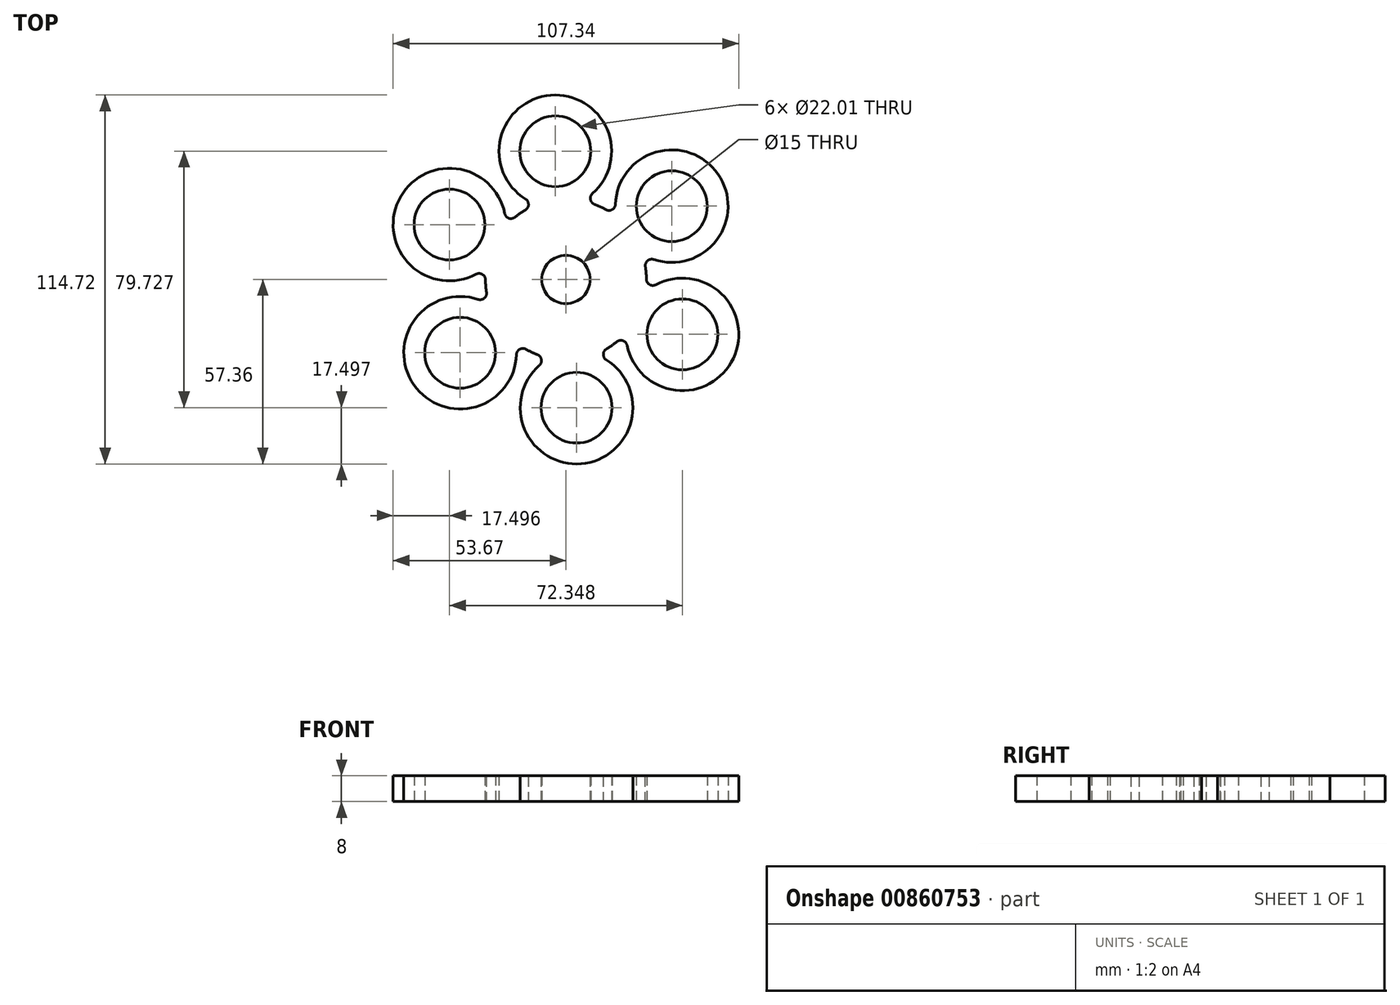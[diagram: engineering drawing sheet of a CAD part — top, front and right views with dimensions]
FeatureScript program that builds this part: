
annotation { "Feature Type Name" : "Feature", "Feature Type Description" : "" }
export const myFeature = defineFeature(function(context is Context, id is Id, definition is map)
    precondition{}
    {
        {
            var Q0;
            Q0=qCreatedBy(makeId("Top.planeOp"),FACE);
            var sketch = newSketch(context, id + "F0", { "sketchPlane" : qUnion([Q0])});
            skCircle(sketch, "E0", {"center": v(0, 0) * mm, "radius": 40 * mm, "construction": true});
            skCircle(sketch, "E1", {"center": v(0, 0) * mm, "radius": 7.5 * mm});
            skLineSegment(sketch, "E2.0", {"start": v(36.17, -17.07) * mm, "end": v(3.3, -39.86) * mm, "construction": true});
            skLineSegment(sketch, "E2.1", {"start": v(3.3, -39.86) * mm, "end": v(-32.87, -22.8) * mm, "construction": true});
            skLineSegment(sketch, "E2.2", {"start": v(-32.87, -22.8) * mm, "end": v(-36.17, 17.07) * mm, "construction": true});
            skLineSegment(sketch, "E2.3", {"start": v(-36.17, 17.07) * mm, "end": v(-3.3, 39.86) * mm, "construction": true});
            skLineSegment(sketch, "E2.4", {"start": v(-3.3, 39.86) * mm, "end": v(32.87, 22.8) * mm, "construction": true});
            skLineSegment(sketch, "E2.5", {"start": v(32.87, 22.8) * mm, "end": v(36.17, -17.07) * mm, "construction": true});
            skArc(sketch, "E3", {"start": v(5.05, 24.48) * mm, "mid": v(-4.75, 57.3) * mm, "end": v(-9, 23.32) * mm});
            skArc(sketch, "E4", {"start": v(-24.7, 3.86) * mm, "mid": v(-24.91, -2.06) * mm, "end": v(-23.73, -7.87) * mm});
            skArc(sketch, "E5.1.0", {"start": v(-18.68, 16.61) * mm, "mid": v(-52, 24.54) * mm, "end": v(-24.7, 3.86) * mm});
            skArc(sketch, "E5.2.0", {"start": v(-23.73, -7.87) * mm, "mid": v(-47.25, -32.76) * mm, "end": v(-15.7, -19.46) * mm});
            skArc(sketch, "E5.3.0", {"start": v(-5.05, -24.48) * mm, "mid": v(4.75, -57.3) * mm, "end": v(9, -23.32) * mm});
            skArc(sketch, "E5.4.0", {"start": v(18.68, -16.61) * mm, "mid": v(52, -24.54) * mm, "end": v(24.7, -3.86) * mm});
            skArc(sketch, "E5.5.0", {"start": v(23.73, 7.87) * mm, "mid": v(47.25, 32.76) * mm, "end": v(15.7, 19.46) * mm});
            skArc(sketch, "E6.trimOffspring", {"start": v(-9, 23.32) * mm, "mid": v(-14.24, 20.54) * mm, "end": v(-18.68, 16.61) * mm});
            skArc(sketch, "E7.trimOffspring", {"start": v(15.7, 19.46) * mm, "mid": v(10.67, 22.6) * mm, "end": v(5.05, 24.48) * mm});
            skArc(sketch, "E8.trimOffspring", {"start": v(24.7, -3.86) * mm, "mid": v(24.91, 2.06) * mm, "end": v(23.73, 7.87) * mm});
            skArc(sketch, "E9.trimOffspring", {"start": v(9, -23.32) * mm, "mid": v(14.24, -20.54) * mm, "end": v(18.68, -16.61) * mm});
            skArc(sketch, "E10.trimOffspring", {"start": v(-15.7, -19.46) * mm, "mid": v(-10.67, -22.6) * mm, "end": v(-5.05, -24.48) * mm});
            skCircle(sketch, "E11", {"center": v(-3.3, 39.86) * mm, "radius": 11 * mm});
            skCircle(sketch, "E12.1.0", {"center": v(-36.17, 17.07) * mm, "radius": 11 * mm});
            skCircle(sketch, "E12.2.0", {"center": v(-32.87, -22.8) * mm, "radius": 11 * mm});
            skCircle(sketch, "E12.3.0", {"center": v(3.3, -39.86) * mm, "radius": 11 * mm});
            skCircle(sketch, "E12.4.0", {"center": v(36.17, -17.07) * mm, "radius": 11 * mm});
            skCircle(sketch, "E12.5.0", {"center": v(32.87, 22.8) * mm, "radius": 11 * mm});
            skSolve(sketch);
        }
        {
            var Q0;
            Q0=makeQuery(id+"F0.imprint","IMPRINT",FACE,{"disambiguationData":[TD([[makeQuery(id+"F0.imprint","IMPRINT",EDGE,{"derivedFrom":sQuery(id+"F0.wireOp",EDGE,"E1")}),-1.0]])]});
            extrude(context, id + "F1", {"entities" : qUnion([Q0]), "depth" : 8 * mm, "offsetDistance" : 25 * mm});
        }
        {
            var Q0;
            Q0=makeQuery(id+"F1.opExtrude","SWEPT_EDGE",EDGE,{"disambiguationData":[OSD([sQuery(id+"F0.wireOp",EDGE,"E5.5.0"),sQuery(id+"F0.wireOp",EDGE,"E7.trimOffspring")])]});
            var Q1;
            Q1=makeQuery(id+"F1.opExtrude","SWEPT_EDGE",EDGE,{"disambiguationData":[OSD([sQuery(id+"F0.wireOp",EDGE,"E3"),sQuery(id+"F0.wireOp",EDGE,"E7.trimOffspring")])]});
            var Q2;
            Q2=makeQuery(id+"F1.opExtrude","SWEPT_EDGE",EDGE,{"disambiguationData":[OSD([sQuery(id+"F0.wireOp",EDGE,"E3"),sQuery(id+"F0.wireOp",EDGE,"E6.trimOffspring")])]});
            var Q3;
            Q3=makeQuery(id+"F1.opExtrude","SWEPT_EDGE",EDGE,{"disambiguationData":[OSD([sQuery(id+"F0.wireOp",EDGE,"E5.1.0"),sQuery(id+"F0.wireOp",EDGE,"E6.trimOffspring")])]});
            var Q4;
            Q4=makeQuery(id+"F1.opExtrude","SWEPT_EDGE",EDGE,{"disambiguationData":[OSD([sQuery(id+"F0.wireOp",EDGE,"E5.4.0"),sQuery(id+"F0.wireOp",EDGE,"E8.trimOffspring")])]});
            var Q5;
            Q5=makeQuery(id+"F1.opExtrude","SWEPT_EDGE",EDGE,{"disambiguationData":[OSD([sQuery(id+"F0.wireOp",EDGE,"E5.5.0"),sQuery(id+"F0.wireOp",EDGE,"E8.trimOffspring")])]});
            var Q6;
            Q6=makeQuery(id+"F1.opExtrude","SWEPT_EDGE",EDGE,{"disambiguationData":[OSD([sQuery(id+"F0.wireOp",EDGE,"E5.4.0"),sQuery(id+"F0.wireOp",EDGE,"E9.trimOffspring")])]});
            var Q7;
            Q7=makeQuery(id+"F1.opExtrude","SWEPT_EDGE",EDGE,{"disambiguationData":[OSD([sQuery(id+"F0.wireOp",EDGE,"E5.3.0"),sQuery(id+"F0.wireOp",EDGE,"E9.trimOffspring")])]});
            var Q8;
            Q8=makeQuery(id+"F1.opExtrude","SWEPT_EDGE",EDGE,{"disambiguationData":[OSD([sQuery(id+"F0.wireOp",EDGE,"E5.3.0"),sQuery(id+"F0.wireOp",EDGE,"E10.trimOffspring")])]});
            var Q9;
            Q9=makeQuery(id+"F1.opExtrude","SWEPT_EDGE",EDGE,{"disambiguationData":[OSD([sQuery(id+"F0.wireOp",EDGE,"E5.2.0"),sQuery(id+"F0.wireOp",EDGE,"E10.trimOffspring")])]});
            var Q10;
            Q10=makeQuery(id+"F1.opExtrude","SWEPT_EDGE",EDGE,{"disambiguationData":[OSD([sQuery(id+"F0.wireOp",EDGE,"E4"),sQuery(id+"F0.wireOp",EDGE,"E5.2.0")])]});
            var Q11;
            Q11=makeQuery(id+"F1.opExtrude","SWEPT_EDGE",EDGE,{"disambiguationData":[OSD([sQuery(id+"F0.wireOp",EDGE,"E4"),sQuery(id+"F0.wireOp",EDGE,"E5.1.0")])]});
            fillet(context, id + "F2", {"entities" : qUnion([Q0, Q1, Q2, Q3, Q4, Q5, Q6, Q7, Q8, Q9, Q10, Q11]), "radius" : 2 * mm, "tangentPropagation" : true, "allowEdgeOverflow" : false});
        }
    });
